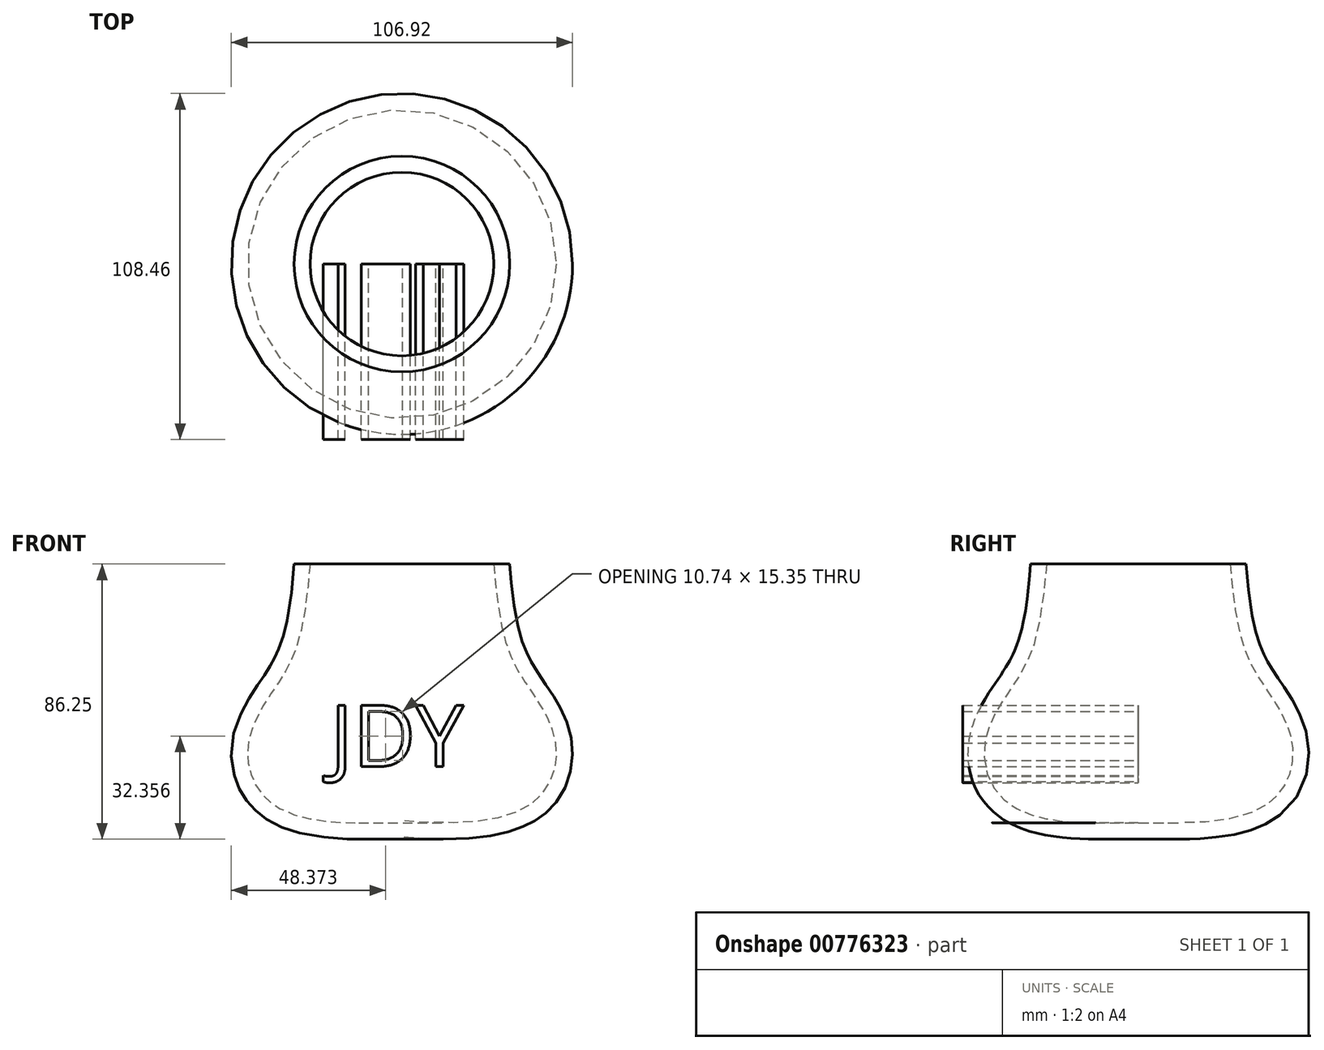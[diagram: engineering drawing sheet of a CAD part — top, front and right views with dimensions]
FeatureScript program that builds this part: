
annotation { "Feature Type Name" : "Feature", "Feature Type Description" : "" }
export const myFeature = defineFeature(function(context is Context, id is Id, definition is map)
    precondition{}
    {
        {
            var Q0;
            Q0=qCreatedBy(makeId("Front.planeOp"),FACE);
            var sketch = newSketch(context, id + "F0", { "sketchPlane" : qUnion([Q0])});
            skFitSpline(sketch, "E0", {"points": [v(28.77, 18.1) * mm, v(34.78, -12.3) * mm, v(44.41, -27.93) * mm, v(48.32, -42.68) * mm, v(39.6, -57.72) * mm, v(-4.93, -61.93) * mm], "startDerivative": vector(15.97, -183.62) * mm, "endDerivative": vector(-204.97, 21.2) * mm});
            skLineSegment(sketch, "E1", {"start": v(-11.55, 18.1) * mm, "end": v(60.36, 18.1) * mm});
            skLineSegment(sketch, "E2", {"start": v(0, 33.14) * mm, "end": v(0, -68.55) * mm});
            skFitSpline(sketch, "E3.0", {"points": [v(33.75, 18.53) * mm, v(34.08, 14.74) * mm, v(34.75, 7.92) * mm, v(35.81, 1.07) * mm, v(36.9, -3.58) * mm, v(37.7, -6.2) * mm, v(38.42, -8.13) * mm, v(39, -9.53) * mm, v(39.64, -10.87) * mm, v(40.34, -12.2) * mm, v(41.1, -13.52) * mm, v(42.18, -15.29) * mm, v(43.64, -17.5) * mm, v(45.49, -20.23) * mm, v(47.04, -22.58) * mm, v(48.24, -24.54) * mm, v(49.4, -26.58) * mm, v(50.7, -29.21) * mm, v(52, -32.53) * mm, v(52.92, -36.02) * mm, v(53.41, -39.66) * mm, v(53.37, -43.45) * mm, v(52.75, -47.3) * mm, v(51.51, -51.11) * mm, v(49.6, -54.8) * mm, v(47.4, -57.64) * mm, v(45.28, -59.71) * mm, v(43.51, -61.14) * mm, v(41.55, -62.43) * mm, v(39.47, -63.55) * mm, v(37.28, -64.5) * mm, v(34.21, -65.6) * mm, v(30.14, -66.63) * mm, v(24.9, -67.46) * mm, v(17.47, -68.06) * mm, v(7.47, -68.02) * mm, v(-1.1, -67.35) * mm, v(-5.44, -66.9) * mm]});
            skSolve(sketch);
        }
        {
            var Q0;
            {var subQ0=sQuery(id+"F0.wireOp",EDGE,"E1");var subQ1=sQuery(id+"F0.wireOp",EDGE,"E0");var subQ2=makeQuery(id+"F0.imprint","INTERSECT",VERTEX,{"derivedFrom":[subQ1,subQ0]});Q0=makeQuery(id+"F0.imprint","IMPRINT",FACE,{"disambiguationData":[TD([[makeQuery(id+"F0.imprint","IMPRINT",EDGE,{"disambiguationData":[TD([[subQ2,-1.0]])],"derivedFrom":subQ1}),1.0]])]});}
            var Q1;
            Q1=sQuery(id+"F0.wireOp",EDGE,"E2");
            revolve(context, id + "F1", {"surfaceOperationType" : NewSurfaceOperationType.NEW, "entities" : qUnion([Q0]), "axis" : qUnion([Q1]), "revolveType" : RevolveType.FULL});
        }
        {
            var Q0;
            Q0=qCreatedBy(makeId("Front.planeOp"),FACE);
            var sketch = newSketch(context, id + "F2", { "sketchPlane" : qUnion([Q0])});
            skText(sketch, "E4", { "text": "JDY", "fontName": "OpenSans-Regular.ttf"});
            const initialGuessF2  = {"E4": [-0.02252, -0.0454, 1, 0, 0.01938]};
            skSetInitialGuess(sketch, initialGuessF2);
            skSolve(sketch);
        }
        {
            var Q0;
            Q0 = qSketchRegion(id + "F2", true);
            extrude(context, id + "F3", {"entities" : qUnion([Q0]), "depth" : 55 * mm, "offsetDistance" : 25 * mm});
        }
    });
